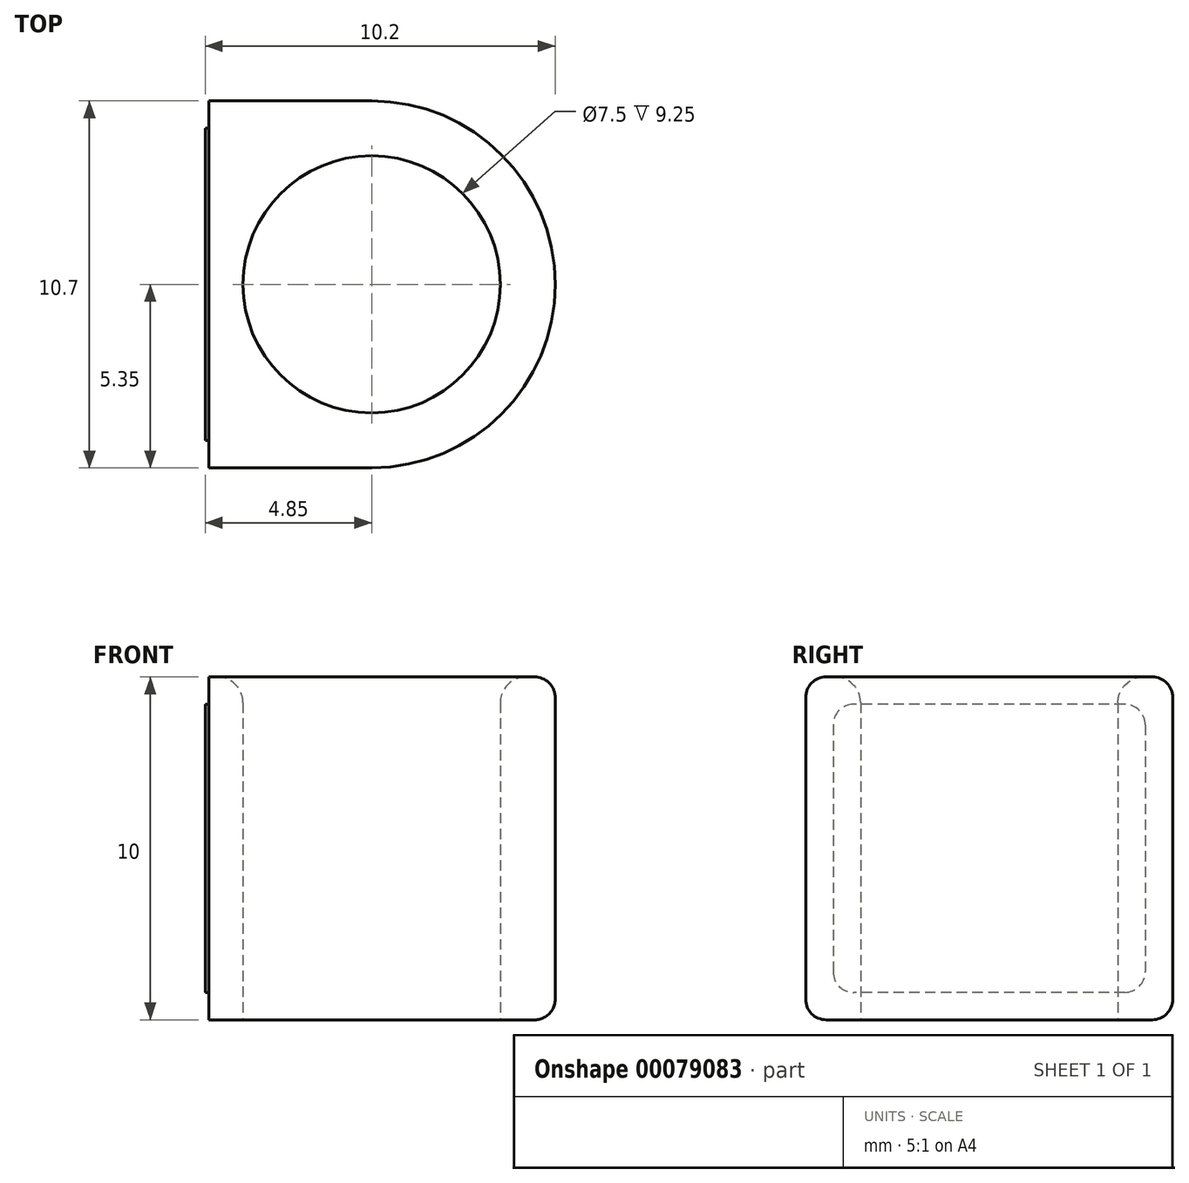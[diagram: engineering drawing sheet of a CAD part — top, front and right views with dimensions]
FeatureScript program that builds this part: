
annotation { "Feature Type Name" : "Feature", "Feature Type Description" : "" }
export const myFeature = defineFeature(function(context is Context, id is Id, definition is map)
    precondition{}
    {
        {
            var Q0;
            Q0=qCreatedBy(makeId("Top.planeOp"),FACE);
            var sketch = newSketch(context, id + "F0", { "sketchPlane" : qUnion([Q0])});
            skCircle(sketch, "E0", {"center": v(0, 0) * mm, "radius": 3.75 * mm});
            skCircle(sketch, "E1", {"center": v(0, 0) * mm, "radius": 5.35 * mm});
            skSolve(sketch);
        }
        {
            var Q0;
            Q0=makeQuery(id+"F0.imprint","IMPRINT",FACE,{"disambiguationData":[TD([[makeQuery(id+"F0.imprint","IMPRINT",EDGE,{"derivedFrom":sQuery(id+"F0.wireOp",EDGE,"E0")}),-1.0]])]});
            var Q1;
            Q1=makeQuery(id+"F0.imprint","IMPRINT",FACE,{"disambiguationData":[TD([[makeQuery(id+"F0.imprint","IMPRINT",EDGE,{"derivedFrom":sQuery(id+"F0.wireOp",EDGE,"E0")}),1.0]])]});
            extrude(context, id + "F1", {"entities" : qUnion([Q0, Q1]), "depth" : 10 * mm});
        }
        {
            var Q0;
            Q0=qCreatedBy(makeId("Right.planeOp"),FACE);
            var sketch = newSketch(context, id + "F2", { "sketchPlane" : qUnion([Q0])});
            skLineSegment(sketch, "E2.bottom", {"start": v(5.35, 10) * mm, "end": v(-5.35, 10) * mm});
            skLineSegment(sketch, "E2.top", {"start": v(5.35, 0) * mm, "end": v(-5.35, 0) * mm});
            skLineSegment(sketch, "E2.left", {"start": v(5.35, 10) * mm, "end": v(5.35, 0) * mm});
            skLineSegment(sketch, "E2.right", {"start": v(-5.35, 10) * mm, "end": v(-5.35, 0) * mm});
            skSolve(sketch);
        }
        {
            var Q0;
            Q0=qSketchRegion(id+"F2",true);
            var Q1;
            Q1=qConstructionFilter(qBodyType(qCreatedBy(id+"F2",EDGE),BodyType.WIRE),ConstructionObject.NO);
            extrude(context, id + "F3", {"entities" : qUnion([Q0]), "operationType" : NewBodyOperationType.ADD, "surfaceEntities" : qUnion([Q1]), "oppositeDirection" : true, "depth" : 4.75 * mm});
        }
        {
            var Q0;
            {var subQ1=sQuery(id+"F2.wireOp",EDGE,"E2.bottom");var subQ2=sQuery(id+"F2.wireOp",EDGE,"E2.top");var subQ3=sQuery(id+"F2.wireOp",EDGE,"E2.left");Q0=makeQuery(id+"F3.boolean.opBoolean","SPLIT",FACE,{"disambiguationData":[TD([makeQuery(id+"F3.opExtrude","SWEPT_FACE",FACE,{"disambiguationData":[OSD([subQ3])]})])],"derivedFrom":makeQuery(id+"F3.opExtrude","CAP_FACE",FACE,{"disambiguationData":[OSD([subQ1,subQ2,subQ3,sQuery(id+"F2.wireOp",EDGE,"E2.right")])],"isStart":false})});}
            var sketch = newSketch(context, id + "F4", { "sketchPlane" : qUnion([Q0])});
            skLineSegment(sketch, "E3.bottom", {"start": v(-5.35, 0) * mm, "end": v(5.35, 0) * mm});
            skLineSegment(sketch, "E3.top", {"start": v(-5.35, 10) * mm, "end": v(5.35, 10) * mm});
            skLineSegment(sketch, "E3.left", {"start": v(-5.35, 0) * mm, "end": v(-5.35, 10) * mm});
            skLineSegment(sketch, "E3.right", {"start": v(5.35, 0) * mm, "end": v(5.35, 10) * mm});
            skSolve(sketch);
        }
        {
            var Q0;
            {var subQ2=sQuery(id+"F4.wireOp",EDGE,"E3.right");Q0=makeQuery(id+"F4.imprint","IMPRINT",FACE,{"disambiguationData":[TD([[makeQuery(id+"F4.imprint","IMPRINT",EDGE,{"derivedFrom":subQ2}),1.0]])]});}
            extrude(context, id + "F5", {"entities" : qUnion([Q0]), "operationType" : NewBodyOperationType.REMOVE, "depth" : 25 * mm});
        }
        {
            var Q0;
            Q0=makeQuery(id+"F0.imprint","IMPRINT",FACE,{"disambiguationData":[TD([[makeQuery(id+"F0.imprint","IMPRINT",EDGE,{"derivedFrom":sQuery(id+"F0.wireOp",EDGE,"E0")}),1.0]])]});
            extrude(context, id + "F6", {"entities" : qUnion([Q0]), "operationType" : NewBodyOperationType.REMOVE, "depth" : 25 * mm});
        }
        {
            var Q0;
            Q0=makeQuery(id+"F3.opExtrude","CAP_FACE",FACE,{"disambiguationData":[OSD([sQuery(id+"F2.wireOp",EDGE,"E2.bottom"),sQuery(id+"F2.wireOp",EDGE,"E2.top"),sQuery(id+"F2.wireOp",EDGE,"E2.left"),sQuery(id+"F2.wireOp",EDGE,"E2.right")])],"isStart":false});
            var sketch = newSketch(context, id + "F7", { "sketchPlane" : qUnion([Q0])});
            skLineSegment(sketch, "E4.0", {"start": v(-4.55, 9.2) * mm, "end": v(-4.55, 0.8) * mm});
            skLineSegment(sketch, "E4.1", {"start": v(-4.55, 9.2) * mm, "end": v(4.55, 9.2) * mm});
            skLineSegment(sketch, "E4.2", {"start": v(4.55, 9.2) * mm, "end": v(4.55, 0.8) * mm});
            skLineSegment(sketch, "E4.3", {"start": v(-4.55, 0.8) * mm, "end": v(4.55, 0.8) * mm});
            skSolve(sketch);
        }
        {
            var Q0;
            Q0=makeQuery(id+"F7.imprint","IMPRINT",FACE,{"disambiguationData":[TD([[makeQuery(id+"F7.imprint","IMPRINT",EDGE,{"derivedFrom":sQuery(id+"F7.wireOp",EDGE,"E4.0")}),1.0]])]});
            extrude(context, id + "F8", {"entities" : qUnion([Q0]), "operationType" : NewBodyOperationType.ADD, "depth" : 0.1 * mm});
        }
        {
            var Q0;
            {var subQ0=sQuery(id+"F2.wireOp",EDGE,"E2.left");var subQ1=sQuery(id+"F2.wireOp",EDGE,"E2.bottom");Q0=makeQuery(id+"F8.boolean.opBoolean","MERGE",EDGE,{"derivedFrom":[makeQuery(id+"F3.opExtrude","SWEPT_EDGE",EDGE,{"disambiguationData":[OSD([subQ1,subQ0])]}),makeQuery(id+"F8.opExtrude","SWEPT_EDGE",EDGE,{"disambiguationData":[OSD([subQ1,subQ0,sQuery(id+"F4.wireOp",EDGE,"E3.top")])]})]});}
            var Q1;
            {var subQ0=sQuery(id+"F2.wireOp",EDGE,"E2.left");var subQ1=sQuery(id+"F2.wireOp",EDGE,"E2.top");Q1=makeQuery(id+"F8.boolean.opBoolean","MERGE",EDGE,{"derivedFrom":[makeQuery(id+"F3.opExtrude","SWEPT_EDGE",EDGE,{"disambiguationData":[OSD([subQ1,subQ0])]}),makeQuery(id+"F8.opExtrude","SWEPT_EDGE",EDGE,{"disambiguationData":[OSD([subQ1,subQ0,sQuery(id+"F4.wireOp",EDGE,"E3.bottom")])]})]});}
            var Q2;
            {var subQ0=sQuery(id+"F2.wireOp",EDGE,"E2.right");var subQ1=sQuery(id+"F2.wireOp",EDGE,"E2.top");Q2=makeQuery(id+"F8.boolean.opBoolean","MERGE",EDGE,{"derivedFrom":[makeQuery(id+"F3.opExtrude","SWEPT_EDGE",EDGE,{"disambiguationData":[OSD([subQ1,subQ0])]}),makeQuery(id+"F8.opExtrude","SWEPT_EDGE",EDGE,{"disambiguationData":[OSD([subQ1,subQ0,sQuery(id+"F4.wireOp",EDGE,"E3.bottom")])]})]});}
            var Q3;
            {var subQ0=sQuery(id+"F2.wireOp",EDGE,"E2.right");var subQ1=sQuery(id+"F2.wireOp",EDGE,"E2.bottom");Q3=makeQuery(id+"F8.boolean.opBoolean","MERGE",EDGE,{"derivedFrom":[makeQuery(id+"F3.opExtrude","SWEPT_EDGE",EDGE,{"disambiguationData":[OSD([subQ1,subQ0])]}),makeQuery(id+"F8.opExtrude","SWEPT_EDGE",EDGE,{"disambiguationData":[OSD([subQ1,subQ0,sQuery(id+"F4.wireOp",EDGE,"E3.top")])]})]});}
            var Q4;
            Q4=makeQuery(id+"F8.opExtrude","SWEPT_EDGE",EDGE,{"disambiguationData":[OSD([sQuery(id+"F7.wireOp",EDGE,"E4.0"),sQuery(id+"F7.wireOp",EDGE,"E4.1")])]});
            var Q5;
            Q5=makeQuery(id+"F8.opExtrude","SWEPT_EDGE",EDGE,{"disambiguationData":[OSD([sQuery(id+"F7.wireOp",EDGE,"E4.1"),sQuery(id+"F7.wireOp",EDGE,"E4.2")])]});
            var Q6;
            Q6=makeQuery(id+"F8.opExtrude","SWEPT_EDGE",EDGE,{"disambiguationData":[OSD([sQuery(id+"F7.wireOp",EDGE,"E4.2"),sQuery(id+"F7.wireOp",EDGE,"E4.3")])]});
            var Q7;
            Q7=makeQuery(id+"F8.opExtrude","SWEPT_EDGE",EDGE,{"disambiguationData":[OSD([sQuery(id+"F7.wireOp",EDGE,"E4.0"),sQuery(id+"F7.wireOp",EDGE,"E4.3")])]});
            fillet(context, id + "F9", {"entities" : qUnion([Q0, Q1, Q2, Q3, Q4, Q5, Q6, Q7]), "radius" : 0.6 * mm, "tangentPropagation" : true, "allowEdgeOverflow" : false});
        }
        {
            var Q0;
            Q0=makeQuery(id+"F6.boolean.opBoolean","COPY",EDGE,{"derivedFrom":makeQuery(id+"F6.opExtrude","CAP_EDGE",EDGE,{"disambiguationData":[OSD([sQuery(id+"F0.wireOp",EDGE,"E0")])],"isStart":true})});
            var Q1;
            Q1=makeQuery(id+"F6.boolean.opBoolean","INTERSECT",EDGE,{"derivedFrom":[makeQuery(id+"F3.boolean.opBoolean","MERGE",FACE,{"derivedFrom":[makeQuery(id+"F1.opExtrude","CAP_FACE",FACE,{"disambiguationData":[OSD([sQuery(id+"F0.wireOp",EDGE,"E1")])],"isStart":false}),makeQuery(id+"F3.opExtrude","SWEPT_FACE",FACE,{"disambiguationData":[OSD([sQuery(id+"F2.wireOp",EDGE,"E2.bottom")])]})]}),makeQuery(id+"F6.opExtrude","SWEPT_FACE",FACE,{"disambiguationData":[OSD([sQuery(id+"F0.wireOp",EDGE,"E0")])]})]});
            fillet(context, id + "F10", {"entities" : qUnion([Q0, Q1]), "radius" : 0.75 * mm, "tangentPropagation" : true, "allowEdgeOverflow" : false});
        }
    });
